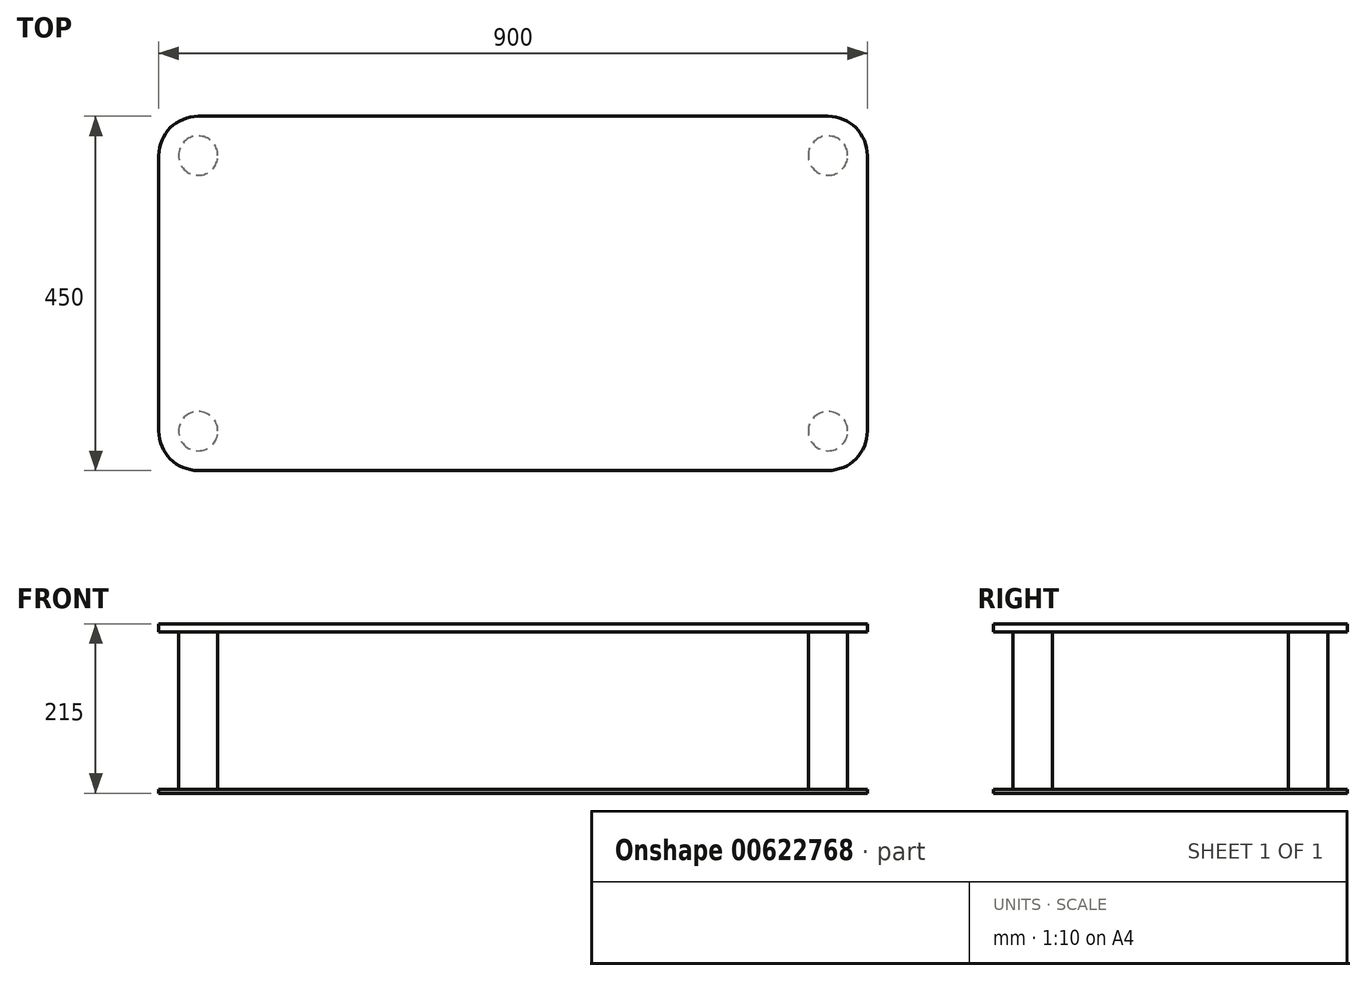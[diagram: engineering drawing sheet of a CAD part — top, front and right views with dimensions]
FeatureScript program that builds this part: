
annotation { "Feature Type Name" : "Feature", "Feature Type Description" : "" }
export const myFeature = defineFeature(function(context is Context, id is Id, definition is map)
    precondition{}
    {
        {
            var Q0;
            Q0=qCreatedBy(makeId("Top.planeOp"),FACE);
            var sketch = newSketch(context, id + "F0", { "sketchPlane" : qUnion([Q0])});
            skLineSegment(sketch, "E0.bottom", {"start": v(-450, 225) * mm, "end": v(450, 225) * mm});
            skLineSegment(sketch, "E0.top", {"start": v(-450, -225) * mm, "end": v(450, -225) * mm});
            skLineSegment(sketch, "E0.left", {"start": v(-450, 225) * mm, "end": v(-450, -225) * mm});
            skLineSegment(sketch, "E0.right", {"start": v(450, 225) * mm, "end": v(450, -225) * mm});
            skLineSegment(sketch, "E1", {"start": v(-450, 225) * mm, "end": v(450, -225) * mm, "construction": true});
            skSolve(sketch);
        }
        {
            var Q0;
            Q0 = qSketchRegion(id + "F0", true);
            extrude(context, id + "F1", {"entities" : qUnion([Q0]), "depth" : 5 * mm, "offsetDistance" : 25.4 * mm});
        }
        {
            var Q0;
            Q0=makeQuery(id+"F1.opExtrude","CAP_FACE",FACE,{"disambiguationData":[OSD([sQuery(id+"F0.wireOp",EDGE,"E0.bottom"),sQuery(id+"F0.wireOp",EDGE,"E0.top"),sQuery(id+"F0.wireOp",EDGE,"E0.left"),sQuery(id+"F0.wireOp",EDGE,"E0.right")])],"isStart":false});
            var sketch = newSketch(context, id + "F2", { "sketchPlane" : qUnion([Q0])});
            skCircle(sketch, "E2", {"center": v(-400, 175) * mm, "radius": 25 * mm});
            skLineSegment(sketch, "E3", {"start": v(0, 0) * mm, "end": v(0, 259.65) * mm, "construction": true});
            skLineSegment(sketch, "E4", {"start": v(0, 0) * mm, "end": v(-520.75, 0) * mm, "construction": true});
            skCircle(sketch, "E5.MirrorC", {"center": v(400, 175) * mm, "radius": 25 * mm});
            skCircle(sketch, "E6.MirrorC", {"center": v(-400, -175) * mm, "radius": 25 * mm});
            skCircle(sketch, "E7.MirrorC", {"center": v(400, -175) * mm, "radius": 25 * mm});
            skSolve(sketch);
        }
        {
            var Q0;
            Q0 = qSketchRegion(id + "F2", true);
            extrude(context, id + "F3", {"entities" : qUnion([Q0]), "operationType" : NewBodyOperationType.ADD, "depth" : 200 * mm, "offsetDistance" : 25 * mm});
        }
        {
            var Q0;
            Q0=makeQuery(id+"F3.opExtrude","CAP_FACE",FACE,{"disambiguationData":[OSD([sQuery(id+"F2.wireOp",EDGE,"E2")])],"isStart":false});
            var sketch = newSketch(context, id + "F4", { "sketchPlane" : qUnion([Q0])});
            skLineSegment(sketch, "E8.0.0", {"start": v(-450, 225) * mm, "end": v(-450, -225) * mm});
            skLineSegment(sketch, "E8.0.1", {"start": v(-450, -225) * mm, "end": v(450, -225) * mm});
            skLineSegment(sketch, "E8.0.2", {"start": v(450, -225) * mm, "end": v(450, 225) * mm});
            skLineSegment(sketch, "E8.0.3", {"start": v(450, 225) * mm, "end": v(-450, 225) * mm});
            skSolve(sketch);
        }
        {
            var Q0;
            Q0 = qSketchRegion(id + "F4", true);
            extrude(context, id + "F5", {"entities" : qUnion([Q0]), "depth" : 10 * mm, "offsetDistance" : 25 * mm});
        }
        {
            var Q0;
            Q0=makeQuery(id+"F1.opExtrude","SWEPT_EDGE",EDGE,{"disambiguationData":[OSD([sQuery(id+"F0.wireOp",EDGE,"E0.top"),sQuery(id+"F0.wireOp",EDGE,"E0.left")])]});
            var Q1;
            Q1=makeQuery(id+"F5.opExtrude","SWEPT_EDGE",EDGE,{"disambiguationData":[OSD([sQuery(id+"F4.wireOp",EDGE,"E8.0.0"),sQuery(id+"F4.wireOp",EDGE,"E8.0.1")])]});
            var Q2;
            Q2=makeQuery(id+"F5.opExtrude","SWEPT_EDGE",EDGE,{"disambiguationData":[OSD([sQuery(id+"F4.wireOp",EDGE,"E8.0.1"),sQuery(id+"F4.wireOp",EDGE,"E8.0.2")])]});
            var Q3;
            Q3=makeQuery(id+"F1.opExtrude","SWEPT_EDGE",EDGE,{"disambiguationData":[OSD([sQuery(id+"F0.wireOp",EDGE,"E0.top"),sQuery(id+"F0.wireOp",EDGE,"E0.right")])]});
            var Q4;
            Q4=makeQuery(id+"F1.opExtrude","SWEPT_EDGE",EDGE,{"disambiguationData":[OSD([sQuery(id+"F0.wireOp",EDGE,"E0.bottom"),sQuery(id+"F0.wireOp",EDGE,"E0.right")])]});
            var Q5;
            Q5=makeQuery(id+"F5.opExtrude","SWEPT_EDGE",EDGE,{"disambiguationData":[OSD([sQuery(id+"F4.wireOp",EDGE,"E8.0.2"),sQuery(id+"F4.wireOp",EDGE,"E8.0.3")])]});
            var Q6;
            Q6=makeQuery(id+"F5.opExtrude","SWEPT_EDGE",EDGE,{"disambiguationData":[OSD([sQuery(id+"F4.wireOp",EDGE,"E8.0.0"),sQuery(id+"F4.wireOp",EDGE,"E8.0.3")])]});
            var Q7;
            Q7=makeQuery(id+"F1.opExtrude","SWEPT_EDGE",EDGE,{"disambiguationData":[OSD([sQuery(id+"F0.wireOp",EDGE,"E0.bottom"),sQuery(id+"F0.wireOp",EDGE,"E0.left")])]});
            fillet(context, id + "F6", {"entities" : qUnion([Q0, Q1, Q2, Q3, Q4, Q5, Q6, Q7]), "radius" : 50 * mm, "tangentPropagation" : true, "allowEdgeOverflow" : false});
        }
    });
